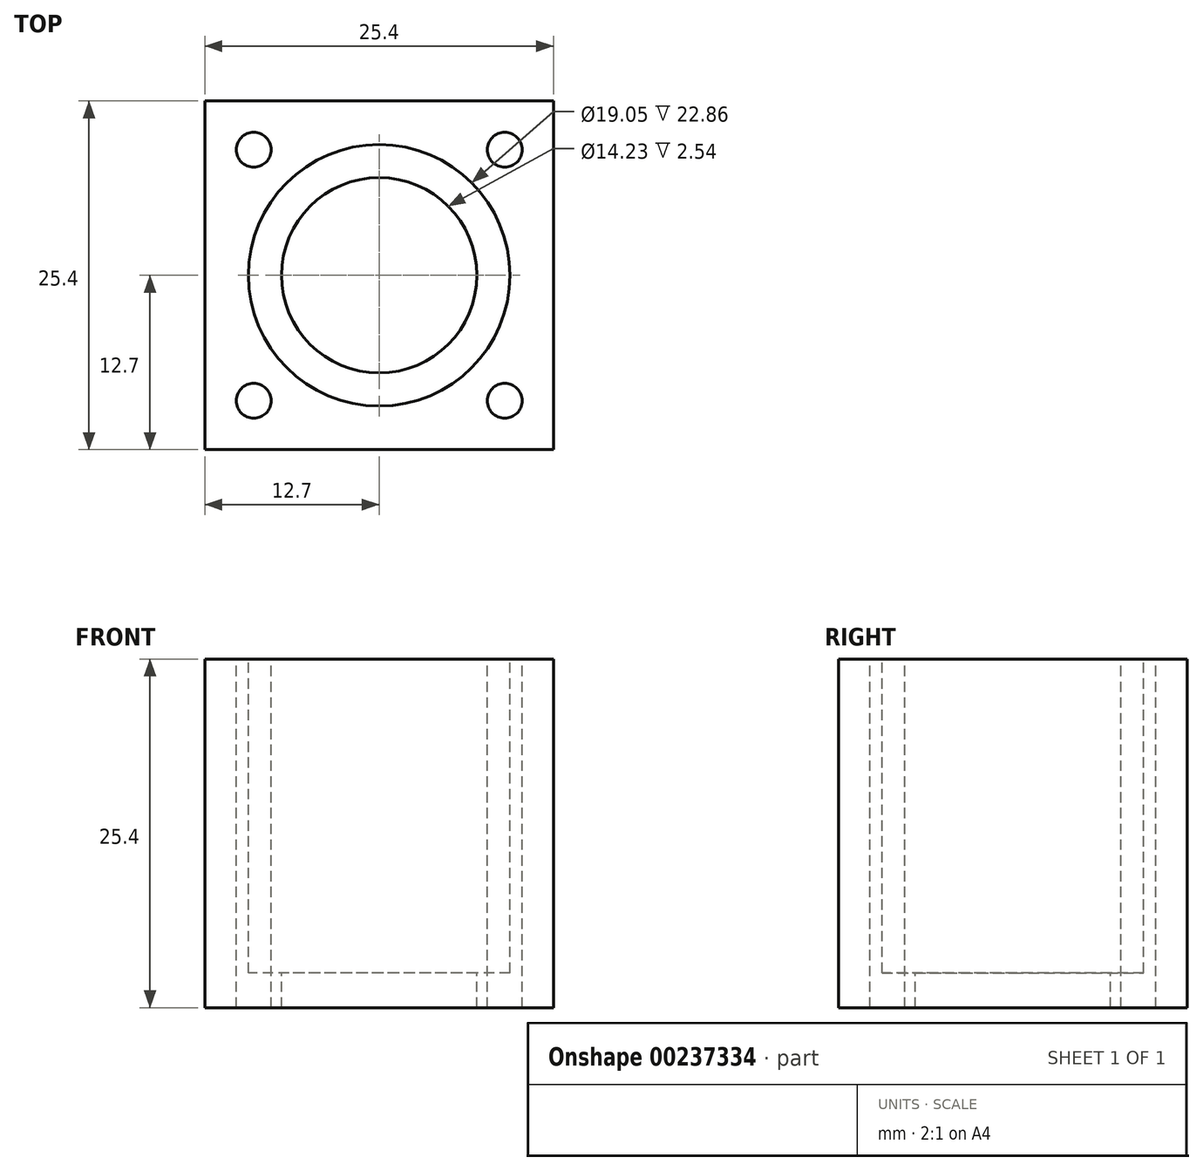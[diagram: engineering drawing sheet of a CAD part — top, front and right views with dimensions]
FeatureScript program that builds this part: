
annotation { "Feature Type Name" : "Feature", "Feature Type Description" : "" }
export const myFeature = defineFeature(function(context is Context, id is Id, definition is map)
    precondition{}
    {
        {
            var Q0;
            Q0=qCreatedBy(makeId("Top.planeOp"),FACE);
            var sketch = newSketch(context, id + "F0", { "sketchPlane" : qUnion([Q0])});
            skLineSegment(sketch, "E0.bottom", {"start": v(0, 0) * mm, "end": v(25.4, 0) * mm});
            skLineSegment(sketch, "E0.top", {"start": v(0, 25.4) * mm, "end": v(25.4, 25.4) * mm});
            skLineSegment(sketch, "E0.left", {"start": v(0, 0) * mm, "end": v(0, 25.4) * mm});
            skLineSegment(sketch, "E0.right", {"start": v(25.4, 0) * mm, "end": v(25.4, 25.4) * mm});
            skSolve(sketch);
        }
        {
            var Q0;
            Q0 = qSketchRegion(id + "F0", true);
            extrude(context, id + "F1", {"entities" : qUnion([Q0]), "depth" : 25.4 * mm});
        }
        {
            var Q0;
            Q0=makeQuery(id+"F1.opExtrude","CAP_FACE",FACE,{"disambiguationData":[OSD([sQuery(id+"F0.wireOp",EDGE,"E0.bottom"),sQuery(id+"F0.wireOp",EDGE,"E0.top"),sQuery(id+"F0.wireOp",EDGE,"E0.left"),sQuery(id+"F0.wireOp",EDGE,"E0.right")])],"isStart":false});
            var sketch = newSketch(context, id + "F2", { "sketchPlane" : qUnion([Q0])});
            skLineSegment(sketch, "E1", {"start": v(0, 12.7) * mm, "end": v(25.4, 12.7) * mm, "construction": true});
            skCircle(sketch, "E2", {"center": v(12.7, 12.7) * mm, "radius": 9.53 * mm});
            skSolve(sketch);
        }
        {
            var Q0;
            Q0 = qSketchRegion(id + "F2", true);
            extrude(context, id + "F3", {"entities" : qUnion([Q0]), "operationType" : NewBodyOperationType.REMOVE, "oppositeDirection" : true, "depth" : 22.86 * mm});
        }
        {
            var Q0;
            Q0=makeQuery(id+"F3.boolean.opBoolean","COPY",FACE,{"derivedFrom":makeQuery(id+"F3.opExtrude","CAP_FACE",FACE,{"disambiguationData":[OSD([sQuery(id+"F2.wireOp",EDGE,"E2")])],"isStart":false})});
            var sketch = newSketch(context, id + "F4", { "sketchPlane" : qUnion([Q0])});
            skCircle(sketch, "E3", {"center": v(12.7, 12.7) * mm, "radius": 7.12 * mm});
            skSolve(sketch);
        }
        {
            var Q0;
            Q0 = qSketchRegion(id + "F4", true);
            extrude(context, id + "F5", {"entities" : qUnion([Q0]), "operationType" : NewBodyOperationType.REMOVE, "endBound" : BoundingType.THROUGH_ALL, "oppositeDirection" : true, "depth" : 25.4 * mm});
        }
        {
            var Q0;
            Q0=makeQuery(id+"F1.opExtrude","CAP_FACE",FACE,{"disambiguationData":[OSD([sQuery(id+"F0.wireOp",EDGE,"E0.bottom"),sQuery(id+"F0.wireOp",EDGE,"E0.top"),sQuery(id+"F0.wireOp",EDGE,"E0.left"),sQuery(id+"F0.wireOp",EDGE,"E0.right")])],"isStart":false});
            var sketch = newSketch(context, id + "F6", { "sketchPlane" : qUnion([Q0])});
            skLineSegment(sketch, "E4.bottom", {"start": v(21.84, 3.56) * mm, "end": v(3.56, 3.56) * mm, "construction": true});
            skLineSegment(sketch, "E4.top", {"start": v(21.84, 21.84) * mm, "end": v(3.56, 21.84) * mm, "construction": true});
            skLineSegment(sketch, "E4.left", {"start": v(21.84, 3.56) * mm, "end": v(21.84, 21.84) * mm, "construction": true});
            skLineSegment(sketch, "E4.right", {"start": v(3.56, 3.56) * mm, "end": v(3.56, 21.84) * mm, "construction": true});
            skPoint(sketch, "E4.middle", {"position": v(12.7, 12.7) * mm});
            skCircle(sketch, "E5", {"center": v(21.84, 3.56) * mm, "radius": 1.27 * mm});
            skCircle(sketch, "E6", {"center": v(21.84, 21.84) * mm, "radius": 1.27 * mm});
            skCircle(sketch, "E7", {"center": v(3.56, 21.84) * mm, "radius": 1.27 * mm});
            skCircle(sketch, "E8", {"center": v(3.56, 3.56) * mm, "radius": 1.27 * mm});
            skSolve(sketch);
        }
        {
            var Q0;
            Q0 = qSketchRegion(id + "F6", true);
            extrude(context, id + "F7", {"entities" : qUnion([Q0]), "operationType" : NewBodyOperationType.REMOVE, "endBound" : BoundingType.THROUGH_ALL, "oppositeDirection" : true, "depth" : 25.4 * mm});
        }
    });
